# Revit family: Clarus_Glide TV Fixed_R20
name_source: partatom
category: Furniture
units: mm (PartAtom-declared; Revit-internal decimal feet)

## family parameters
Cut with Voids When Loaded = No
Host = Face
Room Calculation Point = No
Shared = No

## types (1)
- Horizontal 138" Fixed x (2) 30" Slider x 60" Height
    Default Elevation = 0"
    Depth = 3 3/4"
    Description = For years, the fixed walls of modern office spaces have been steadily removed to create an open environment. Glide is the next step in the revolution, maximizing existing wall space to provide hundreds of consolidated square feet of glass writing surface and inspire personal communication and collaboration.
    Fixed Panel Height = 57 1/2"
    Fixed Panel Width = 138"
    Hardware = Clarus Hardware
    Manufacturer = Clarus
    Model = Glide
    Modeled By = Commense Studio
    Product URL = https://www.clarus.com
    Sliding Panel Height = 60"
    Sliding Panel Width = 30"
    URL = https://www.clarus.com

## geometry (parser evidence)
native form markers: Blend x8, Sweep x10
no freeform markers — native parametric forms only
